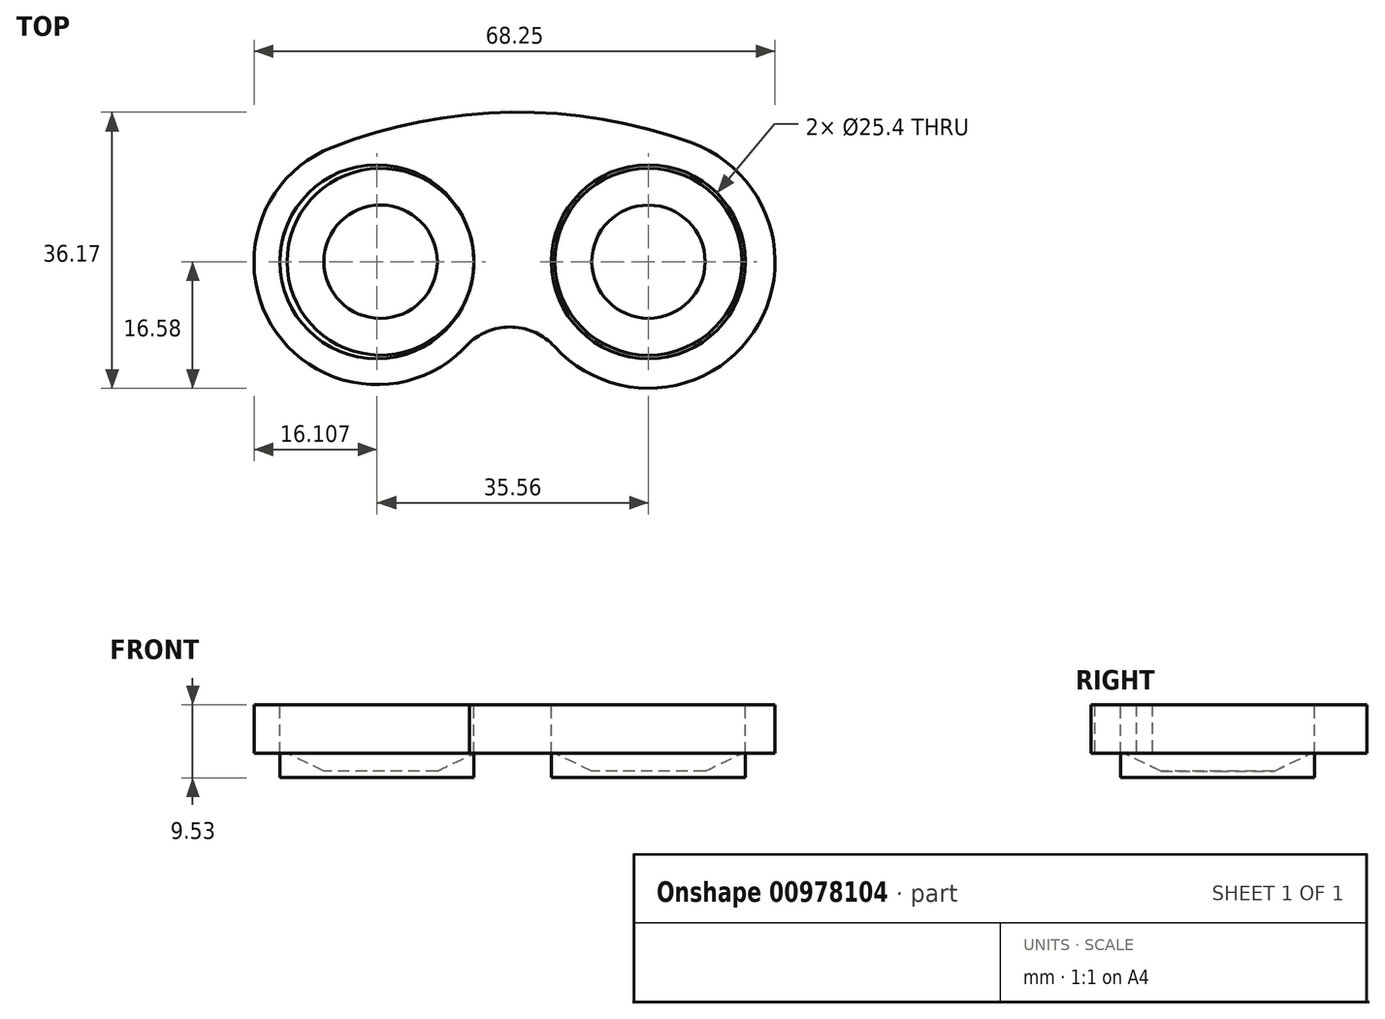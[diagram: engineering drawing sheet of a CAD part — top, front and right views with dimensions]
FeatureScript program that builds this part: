
annotation { "Feature Type Name" : "Feature", "Feature Type Description" : "" }
export const myFeature = defineFeature(function(context is Context, id is Id, definition is map)
    precondition{}
    {
        {
            var Q0;
            Q0=qCreatedBy(makeId("Top.planeOp"),FACE);
            var sketch = newSketch(context, id + "F0", { "sketchPlane" : qUnion([Q0])});
            skArc(sketch, "E0", {"start": v(13.87, 15.58) * mm, "mid": v(-9.73, 19.59) * mm, "end": v(-33.23, 15) * mm});
            skPoint(sketch, "E0.first.point", {"position": v(-27.35, 16.99) * mm});
            skPoint(sketch, "E0.second.point", {"position": v(8.2, 17.36) * mm});
            skPoint(sketch, "E0.third.point", {"position": v(-8.12, 19.59) * mm});
            skArc(sketch, "E1", {"start": v(-33.23, 15) * mm, "mid": v(-40.54, -9.25) * mm, "end": v(-15.26, -10.64) * mm});
            skArc(sketch, "E2", {"start": v(-4.08, -11.14) * mm, "mid": v(21.97, -9.25) * mm, "end": v(13.87, 15.58) * mm});
            skArc(sketch, "E3", {"start": v(-18.94, -13.73) * mm, "mid": v(-19.88, -14.2) * mm, "end": v(-20.8, -14.72) * mm});
            skPoint(sketch, "E3.first.point", {"position": v(-27.35, -20.52) * mm});
            skPoint(sketch, "E3.second.point", {"position": v(8.2, -19.96) * mm});
            skPoint(sketch, "E3.third.point", {"position": v(-18.94, -13.73) * mm});
            skArc(sketch, "E4", {"start": v(-4.06, -11.15) * mm, "mid": v(-10.12, -8.56) * mm, "end": v(-16.03, -11.46) * mm});
            skPoint(sketch, "E4.first.point", {"position": v(-16.03, -11.46) * mm});
            skPoint(sketch, "E4.second.point", {"position": v(-4.06, -11.15) * mm});
            skPoint(sketch, "E4.third.point", {"position": v(-9.37, -8.57) * mm});
            skSolve(sketch);
        }
        {
            var Q0;
            Q0 = qSketchRegion(id + "F0", true);
            extrude(context, id + "F1", {"entities" : qUnion([Q0]), "depth" : 6.35 * mm, "offsetDistance" : 25.4 * mm});
        }
        {
            var Q0;
            Q0=makeQuery(id+"F1.opExtrude","CAP_FACE",FACE,{"disambiguationData":[OSD([sQuery(id+"F0.wireOp",EDGE,"E0"),sQuery(id+"F0.wireOp",EDGE,"E1"),sQuery(id+"F0.wireOp",EDGE,"E2"),sQuery(id+"F0.wireOp",EDGE,"E4")])],"isStart":true});
            var sketch = newSketch(context, id + "F2", { "sketchPlane" : qUnion([Q0])});
            skCircle(sketch, "E5", {"center": v(-27.35, 0) * mm, "radius": 12.7 * mm});
            skCircle(sketch, "E6", {"center": v(8.2, 0) * mm, "radius": 12.7 * mm});
            skSolve(sketch);
        }
        {
            var Q0;
            Q0 = qSketchRegion(id + "F2", true);
            extrude(context, id + "F3", {"entities" : qUnion([Q0]), "operationType" : NewBodyOperationType.ADD, "depth" : 3.17 * mm, "offsetDistance" : 25.4 * mm});
        }
        {
            var Q0;
            Q0=qCreatedBy(makeId("Front.planeOp"),FACE);
            var sketch = newSketch(context, id + "F4", { "sketchPlane" : qUnion([Q0])});
            skLineSegment(sketch, "E7", {"start": v(-26.88, -2.3) * mm, "end": v(-26.88, 0) * mm});
            skLineSegment(sketch, "E8", {"start": v(-26.88, 0) * mm, "end": v(-39.12, 0) * mm});
            skLineSegment(sketch, "E9", {"start": v(-39.12, 0) * mm, "end": v(-34.3, -2.3) * mm});
            skLineSegment(sketch, "E10", {"start": v(-26.88, 0) * mm, "end": v(-26.88, 5.27) * mm});
            skLineSegment(sketch, "E11", {"start": v(-26.88, -2.3) * mm, "end": v(-34.3, -2.3) * mm});
            skPoint(sketch, "E12.start.orphan", {"position": v(-32.48, -3.17) * mm});
            skPoint(sketch, "E13.orphan", {"position": v(-26.88, -3.17) * mm});
            skSolve(sketch);
        }
        {
            var Q0;
            Q0 = qSketchRegion(id + "F4", true);
            var Q1;
            Q1=sQuery(id+"F4.wireOp",EDGE,"E10");
            revolve(context, id + "F5", {"operationType" : NewBodyOperationType.REMOVE, "surfaceOperationType" : NewSurfaceOperationType.NEW, "entities" : qUnion([Q0]), "axis" : qUnion([Q1]), "revolveType" : RevolveType.FULL, "oppositeDirection" : true});
        }
        {
            var Q0;
            Q0=makeQuery(id+"F1.opExtrude","CAP_FACE",FACE,{"disambiguationData":[OSD([sQuery(id+"F0.wireOp",EDGE,"E0"),sQuery(id+"F0.wireOp",EDGE,"E1"),sQuery(id+"F0.wireOp",EDGE,"E2"),sQuery(id+"F0.wireOp",EDGE,"E4")])],"isStart":false});
            var sketch = newSketch(context, id + "F6", { "sketchPlane" : qUnion([Q0])});
            skCircle(sketch, "E14", {"center": v(-27.35, 0) * mm, "radius": 12.7 * mm});
            skSolve(sketch);
        }
        {
            var Q0;
            Q0 = qSketchRegion(id + "F6", true);
            extrude(context, id + "F7", {"entities" : qUnion([Q0]), "operationType" : NewBodyOperationType.REMOVE, "oppositeDirection" : true, "depth" : 6.35 * mm, "offsetDistance" : 25.4 * mm});
        }
        {
            var Q0;
            Q0=qCreatedBy(makeId("Front.planeOp"),FACE);
            var sketch = newSketch(context, id + "F8", { "sketchPlane" : qUnion([Q0])});
            skLineSegment(sketch, "E15", {"start": v(0, 0) * mm, "end": v(8.2, 0) * mm});
            skLineSegment(sketch, "E16", {"start": v(8.2, 0) * mm, "end": v(8.2, -2.31) * mm});
            skLineSegment(sketch, "E17", {"start": v(8.2, -2.31) * mm, "end": v(0.79, -2.31) * mm});
            skLineSegment(sketch, "E18", {"start": v(8.2, 0) * mm, "end": v(-4.04, 0) * mm});
            skLineSegment(sketch, "E19", {"start": v(-4.04, 0) * mm, "end": v(0.79, -2.31) * mm});
            skLineSegment(sketch, "E20", {"start": v(8.2, 0) * mm, "end": v(8.2, 5.2) * mm});
            skSolve(sketch);
        }
        {
            var Q0;
            Q0 = qSketchRegion(id + "F8", true);
            var Q1;
            Q1=sQuery(id+"F8.wireOp",EDGE,"E20");
            revolve(context, id + "F9", {"operationType" : NewBodyOperationType.REMOVE, "surfaceOperationType" : NewSurfaceOperationType.NEW, "entities" : qUnion([Q0]), "axis" : qUnion([Q1]), "revolveType" : RevolveType.FULL, "oppositeDirection" : true});
        }
        {
            var Q0;
            Q0=makeQuery(id+"F1.opExtrude","CAP_FACE",FACE,{"disambiguationData":[OSD([sQuery(id+"F0.wireOp",EDGE,"E0"),sQuery(id+"F0.wireOp",EDGE,"E1"),sQuery(id+"F0.wireOp",EDGE,"E2"),sQuery(id+"F0.wireOp",EDGE,"E4")])],"isStart":false});
            var sketch = newSketch(context, id + "F10", { "sketchPlane" : qUnion([Q0])});
            skCircle(sketch, "E21", {"center": v(8.2, 0) * mm, "radius": 12.7 * mm});
            skSolve(sketch);
        }
        {
            var Q0;
            Q0 = qSketchRegion(id + "F10", true);
            extrude(context, id + "F11", {"entities" : qUnion([Q0]), "operationType" : NewBodyOperationType.REMOVE, "oppositeDirection" : true, "depth" : 6.35 * mm, "offsetDistance" : 25.4 * mm});
        }
    });
